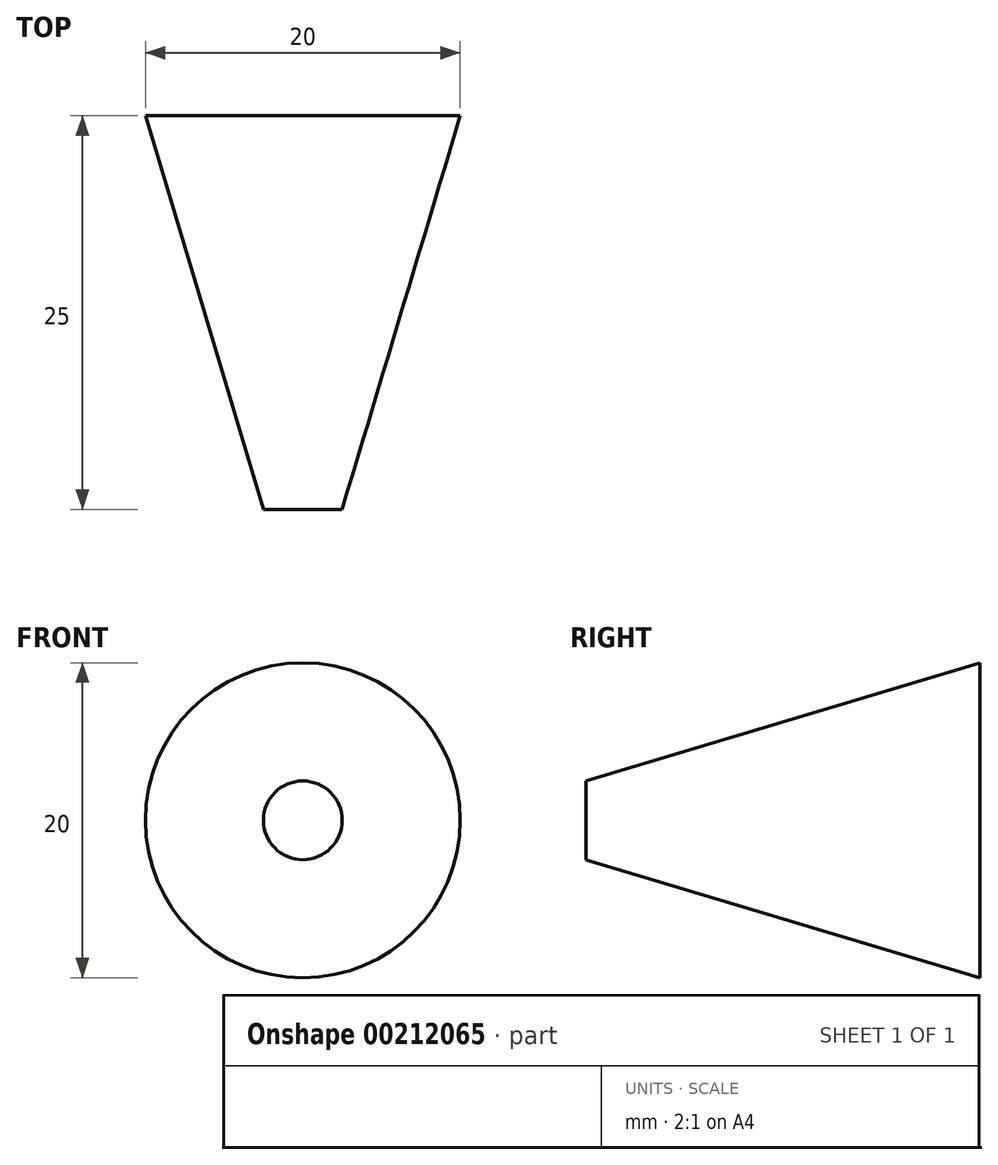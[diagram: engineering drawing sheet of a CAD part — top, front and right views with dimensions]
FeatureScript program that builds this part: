
annotation { "Feature Type Name" : "Feature", "Feature Type Description" : "" }
export const myFeature = defineFeature(function(context is Context, id is Id, definition is map)
    precondition{}
    {
        {
            var Q0;
            Q0=qCreatedBy(makeId("Front.planeOp"),FACE);
            var sketch = newSketch(context, id + "F0", { "sketchPlane" : qUnion([Q0])});
            skCircle(sketch, "E0", {"center": v(0, 0) * mm, "radius": 10 * mm});
            skSolve(sketch);
        }
        {
            var Q0;
            Q0=qCreatedBy(makeId("Front.planeOp"),FACE);
            cPlane(context, id + "F1", {"entities" : qUnion([Q0]), "cplaneType" : CPlaneType.OFFSET, "offset" : 25 * mm, "width" : 150 * mm, "height" : 150 * mm});
        }
        {
            var Q0;
            Q0=qCreatedBy(id+"F1.planeOp",FACE);
            var sketch = newSketch(context, id + "F2", { "sketchPlane" : qUnion([Q0])});
            skCircle(sketch, "E1", {"center": v(0, 0) * mm, "radius": 2.5 * mm});
            skSolve(sketch);
        }
        {
            var Q0;
            Q0=makeQuery(id+"F2.imprint","IMPRINT",FACE,{"disambiguationData":[TD([[makeQuery(id+"F2.imprint","IMPRINT",EDGE,{"derivedFrom":sQuery(id+"F2.wireOp",EDGE,"E1")}),1.0]])]});
            var Q1;
            Q1=makeQuery(id+"F0.imprint","IMPRINT",FACE,{"disambiguationData":[TD([[makeQuery(id+"F0.imprint","IMPRINT",EDGE,{"derivedFrom":sQuery(id+"F0.wireOp",EDGE,"E0")}),1.0]])]});
            var Q2;
            Q2=sQuery(id+"F2.wireOp",EDGE,"E1");
            var Q3;
            Q3=sQuery(id+"F0.wireOp",EDGE,"E0");
            loft(context, id + "F3", {"bodyType" : ToolBodyType.SURFACE, "sheetProfilesArray" : [{ "sheetProfileEntities" : qUnion([Q0]) }, { "sheetProfileEntities" : qUnion([Q1]) }], "wireProfilesArray" : [{ "wireProfileEntities" : qUnion([Q2]) }, { "wireProfileEntities" : qUnion([Q3]) }]});
        }
    });
